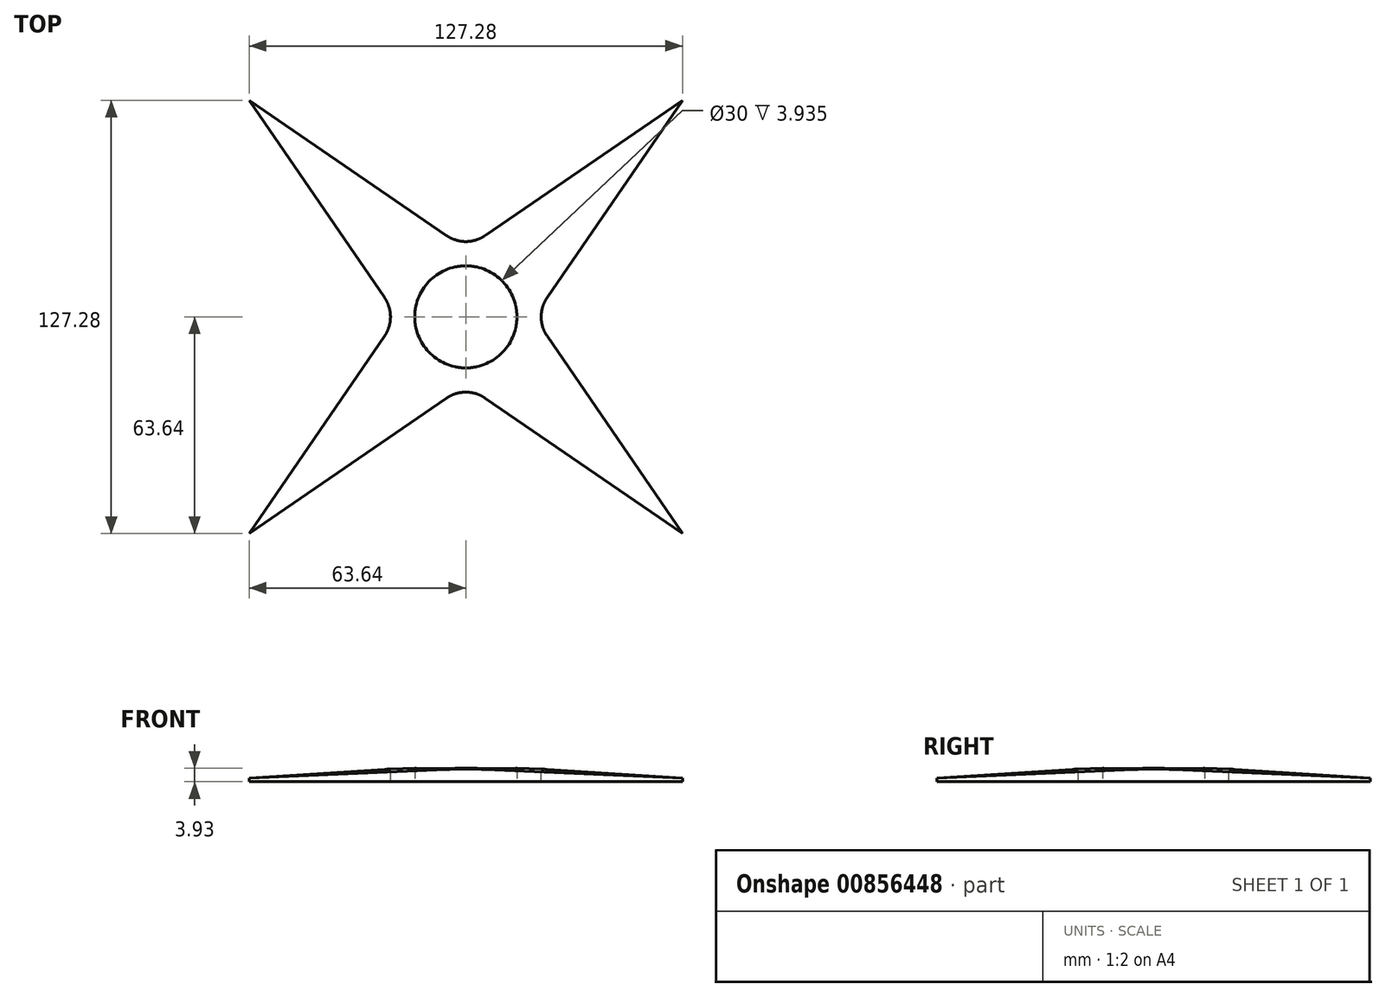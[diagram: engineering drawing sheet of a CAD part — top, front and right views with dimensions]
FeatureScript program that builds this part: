
annotation { "Feature Type Name" : "Feature", "Feature Type Description" : "" }
export const myFeature = defineFeature(function(context is Context, id is Id, definition is map)
    precondition{}
    {
        {
            var Q0;
            Q0=qCreatedBy(makeId("Top.planeOp"),FACE);
            var sketch = newSketch(context, id + "F0", { "sketchPlane" : qUnion([Q0])});
            skLineSegment(sketch, "E0", {"start": v(0, 0) * mm, "end": v(20, 0) * mm});
            skLineSegment(sketch, "E1", {"start": v(20, 0) * mm, "end": v(63.64, 63.64) * mm});
            skLineSegment(sketch, "E2", {"start": v(63.64, 63.64) * mm, "end": v(0, 20) * mm});
            skLineSegment(sketch, "E3", {"start": v(0, 20) * mm, "end": v(0, 0) * mm});
            skLineSegment(sketch, "E4", {"start": v(0, 0) * mm, "end": v(63.64, 63.64) * mm, "construction": true});
            skSolve(sketch);
        }
        {
            var Q0;
            Q0 = qSketchRegion(id + "F0", true);
            extrude(context, id + "F1", {"entities" : qUnion([Q0]), "depth" : 4 * mm, "offsetDistance" : 25 * mm});
        }
        {
            var Q0;
            Q0=qCreatedBy(makeId("Front.planeOp"),FACE);
            var Q1;
            Q1=qCreatedBy(makeId("Right.planeOp"),FACE);
            cPlane(context, id + "F2", {"entities" : qUnion([Q0, Q1]), "cplaneType" : CPlaneType.MID_PLANE, "offset" : 25 * mm, "flipAlignment" : true, "width" : 150 * mm, "height" : 150 * mm});
        }
        {
            var Q0;
            Q0=qCreatedBy(id+"F2.planeOp",FACE);
            var sketch = newSketch(context, id + "F3", { "sketchPlane" : qUnion([Q0])});
            skLineSegment(sketch, "E5", {"start": v(10, 4) * mm, "end": v(90, 1) * mm});
            skLineSegment(sketch, "E6", {"start": v(90, 1) * mm, "end": v(90, 4) * mm});
            skLineSegment(sketch, "E7", {"start": v(90, 4) * mm, "end": v(10, 4) * mm});
            skSolve(sketch);
        }
        {
            var Q0;
            Q0 = qSketchRegion(id + "F3", true);
            extrude(context, id + "F4", {"entities" : qUnion([Q0]), "operationType" : NewBodyOperationType.REMOVE, "endBound" : BoundingType.SYMMETRIC, "depth" : 60 * mm, "offsetDistance" : 25 * mm});
        }
        {
            var Q0;
            Q0=qCreatedBy(makeId("Top.planeOp"),FACE);
            var sketch = newSketch(context, id + "F5", { "sketchPlane" : qUnion([Q0])});
            skCircle(sketch, "E8", {"center": v(0, 0) * mm, "radius": 15 * mm});
            skSolve(sketch);
        }
        {
            var Q0;
            Q0=makeQuery(id+"F5.imprint","IMPRINT",FACE,{"disambiguationData":[TD([[makeQuery(id+"F5.imprint","IMPRINT",EDGE,{"derivedFrom":sQuery(id+"F5.wireOp",EDGE,"E8")}),1.0]])]});
            extrude(context, id + "F6", {"entities" : qUnion([Q0]), "operationType" : NewBodyOperationType.REMOVE, "depth" : 25 * mm, "offsetDistance" : 25 * mm});
        }
        {
            var Q0;
            Q0=makeQuery(id+"F1.opExtrude","SWEPT_BODY",BODY,{"disambiguationData":[OSD([sQuery(id+"F0.wireOp",EDGE,"E0"),sQuery(id+"F0.wireOp",EDGE,"E1"),sQuery(id+"F0.wireOp",EDGE,"E2"),sQuery(id+"F0.wireOp",EDGE,"E3")])]});
            var Q1;
            Q1=makeQuery(id+"F6.boolean.opBoolean","COPY",FACE,{"derivedFrom":makeQuery(id+"F6.opExtrude","SWEPT_FACE",FACE,{"disambiguationData":[OSD([sQuery(id+"F5.wireOp",EDGE,"E8")])]})});
            circularPattern(context, id + "F7", {"operationType" : NewBodyOperationType.ADD, "entities" : qUnion([Q0]), "axis" : qUnion([Q1]), "angle" : 360 * degree, "instanceCount" : 4, "equalSpace" : true});
        }
        {
            var Q0;
            Q0=makeQuery(id+"F7.boolean.opBoolean","MERGE",EDGE,{"derivedFrom":[makeQuery(id+"F1.opExtrude","SWEPT_EDGE",EDGE,{"disambiguationData":[OSD([sQuery(id+"F0.wireOp",EDGE,"E0"),sQuery(id+"F0.wireOp",EDGE,"E1")])]}),makeQuery(id+"F7.opPattern","COPY",EDGE,{"derivedFrom":makeQuery(id+"F1.opExtrude","SWEPT_EDGE",EDGE,{"disambiguationData":[OSD([sQuery(id+"F0.wireOp",EDGE,"E2"),sQuery(id+"F0.wireOp",EDGE,"E3")])]}),"instanceName":"3"})]});
            var Q1;
            Q1=makeQuery(id+"F7.boolean.opBoolean","MERGE",EDGE,{"derivedFrom":[makeQuery(id+"F1.opExtrude","SWEPT_EDGE",EDGE,{"disambiguationData":[OSD([sQuery(id+"F0.wireOp",EDGE,"E2"),sQuery(id+"F0.wireOp",EDGE,"E3")])]}),makeQuery(id+"F7.opPattern","COPY",EDGE,{"derivedFrom":makeQuery(id+"F1.opExtrude","SWEPT_EDGE",EDGE,{"disambiguationData":[OSD([sQuery(id+"F0.wireOp",EDGE,"E0"),sQuery(id+"F0.wireOp",EDGE,"E1")])]}),"instanceName":"1"})]});
            var Q2;
            Q2=makeQuery(id+"F7.boolean.opBoolean","MERGE",EDGE,{"derivedFrom":[makeQuery(id+"F7.opPattern","COPY",EDGE,{"derivedFrom":makeQuery(id+"F1.opExtrude","SWEPT_EDGE",EDGE,{"disambiguationData":[OSD([sQuery(id+"F0.wireOp",EDGE,"E2"),sQuery(id+"F0.wireOp",EDGE,"E3")])]}),"instanceName":"2"}),makeQuery(id+"F7.opPattern","COPY",EDGE,{"derivedFrom":makeQuery(id+"F1.opExtrude","SWEPT_EDGE",EDGE,{"disambiguationData":[OSD([sQuery(id+"F0.wireOp",EDGE,"E0"),sQuery(id+"F0.wireOp",EDGE,"E1")])]}),"instanceName":"3"})]});
            var Q3;
            Q3=makeQuery(id+"F7.boolean.opBoolean","MERGE",EDGE,{"derivedFrom":[makeQuery(id+"F7.opPattern","COPY",EDGE,{"derivedFrom":makeQuery(id+"F1.opExtrude","SWEPT_EDGE",EDGE,{"disambiguationData":[OSD([sQuery(id+"F0.wireOp",EDGE,"E2"),sQuery(id+"F0.wireOp",EDGE,"E3")])]}),"instanceName":"1"}),makeQuery(id+"F7.opPattern","COPY",EDGE,{"derivedFrom":makeQuery(id+"F1.opExtrude","SWEPT_EDGE",EDGE,{"disambiguationData":[OSD([sQuery(id+"F0.wireOp",EDGE,"E0"),sQuery(id+"F0.wireOp",EDGE,"E1")])]}),"instanceName":"2"})]});
            fillet(context, id + "F8", {"entities" : qUnion([Q0, Q1, Q2, Q3]), "radius" : 10 * mm, "tangentPropagation" : true, "allowEdgeOverflow" : false});
        }
        {
            var Q0;
            {var subQ0=makeQuery(id+"F4.opExtrude","SWEPT_FACE",FACE,{"disambiguationData":[OSD([sQuery(id+"F3.wireOp",EDGE,"E5")])]});Q0=makeQuery(id+"F7.boolean.opBoolean","MERGE",EDGE,{"derivedFrom":[makeQuery(id+"F7.opPattern","COPY",EDGE,{"derivedFrom":makeQuery(id+"F4.boolean.opBoolean","INTERSECT",EDGE,{"derivedFrom":[makeQuery(id+"F1.opExtrude","SWEPT_FACE",FACE,{"disambiguationData":[OSD([sQuery(id+"F0.wireOp",EDGE,"E3")])]}),subQ0]}),"instanceName":"1"}),makeQuery(id+"F7.opPattern","COPY",EDGE,{"derivedFrom":makeQuery(id+"F4.boolean.opBoolean","INTERSECT",EDGE,{"derivedFrom":[makeQuery(id+"F1.opExtrude","SWEPT_FACE",FACE,{"disambiguationData":[OSD([sQuery(id+"F0.wireOp",EDGE,"E0")])]}),subQ0]}),"instanceName":"2"})]});}
            var Q1;
            {var subQ0=makeQuery(id+"F4.opExtrude","SWEPT_FACE",FACE,{"disambiguationData":[OSD([sQuery(id+"F3.wireOp",EDGE,"E5")])]});Q1=makeQuery(id+"F7.boolean.opBoolean","MERGE",EDGE,{"derivedFrom":[makeQuery(id+"F7.opPattern","COPY",EDGE,{"derivedFrom":makeQuery(id+"F4.boolean.opBoolean","INTERSECT",EDGE,{"derivedFrom":[makeQuery(id+"F1.opExtrude","SWEPT_FACE",FACE,{"disambiguationData":[OSD([sQuery(id+"F0.wireOp",EDGE,"E3")])]}),subQ0]}),"instanceName":"2"}),makeQuery(id+"F7.opPattern","COPY",EDGE,{"derivedFrom":makeQuery(id+"F4.boolean.opBoolean","INTERSECT",EDGE,{"derivedFrom":[makeQuery(id+"F1.opExtrude","SWEPT_FACE",FACE,{"disambiguationData":[OSD([sQuery(id+"F0.wireOp",EDGE,"E0")])]}),subQ0]}),"instanceName":"3"})]});}
            var Q2;
            {var subQ0=makeQuery(id+"F4.opExtrude","SWEPT_FACE",FACE,{"disambiguationData":[OSD([sQuery(id+"F3.wireOp",EDGE,"E5")])]});Q2=makeQuery(id+"F7.boolean.opBoolean","MERGE",EDGE,{"derivedFrom":[makeQuery(id+"F4.boolean.opBoolean","INTERSECT",EDGE,{"derivedFrom":[makeQuery(id+"F1.opExtrude","SWEPT_FACE",FACE,{"disambiguationData":[OSD([sQuery(id+"F0.wireOp",EDGE,"E0")])]}),subQ0]}),makeQuery(id+"F7.opPattern","COPY",EDGE,{"derivedFrom":makeQuery(id+"F4.boolean.opBoolean","INTERSECT",EDGE,{"derivedFrom":[makeQuery(id+"F1.opExtrude","SWEPT_FACE",FACE,{"disambiguationData":[OSD([sQuery(id+"F0.wireOp",EDGE,"E3")])]}),subQ0]}),"instanceName":"3"})]});}
            var Q3;
            {var subQ0=makeQuery(id+"F4.opExtrude","SWEPT_FACE",FACE,{"disambiguationData":[OSD([sQuery(id+"F3.wireOp",EDGE,"E5")])]});Q3=makeQuery(id+"F7.boolean.opBoolean","MERGE",EDGE,{"derivedFrom":[makeQuery(id+"F4.boolean.opBoolean","INTERSECT",EDGE,{"derivedFrom":[makeQuery(id+"F1.opExtrude","SWEPT_FACE",FACE,{"disambiguationData":[OSD([sQuery(id+"F0.wireOp",EDGE,"E3")])]}),subQ0]}),makeQuery(id+"F7.opPattern","COPY",EDGE,{"derivedFrom":makeQuery(id+"F4.boolean.opBoolean","INTERSECT",EDGE,{"derivedFrom":[makeQuery(id+"F1.opExtrude","SWEPT_FACE",FACE,{"disambiguationData":[OSD([sQuery(id+"F0.wireOp",EDGE,"E0")])]}),subQ0]}),"instanceName":"1"})]});}
            fillet(context, id + "F9", {"entities" : qUnion([Q0, Q1, Q2, Q3]), "radius" : 120 * mm, "tangentPropagation" : true, "allowEdgeOverflow" : false});
        }
    });
